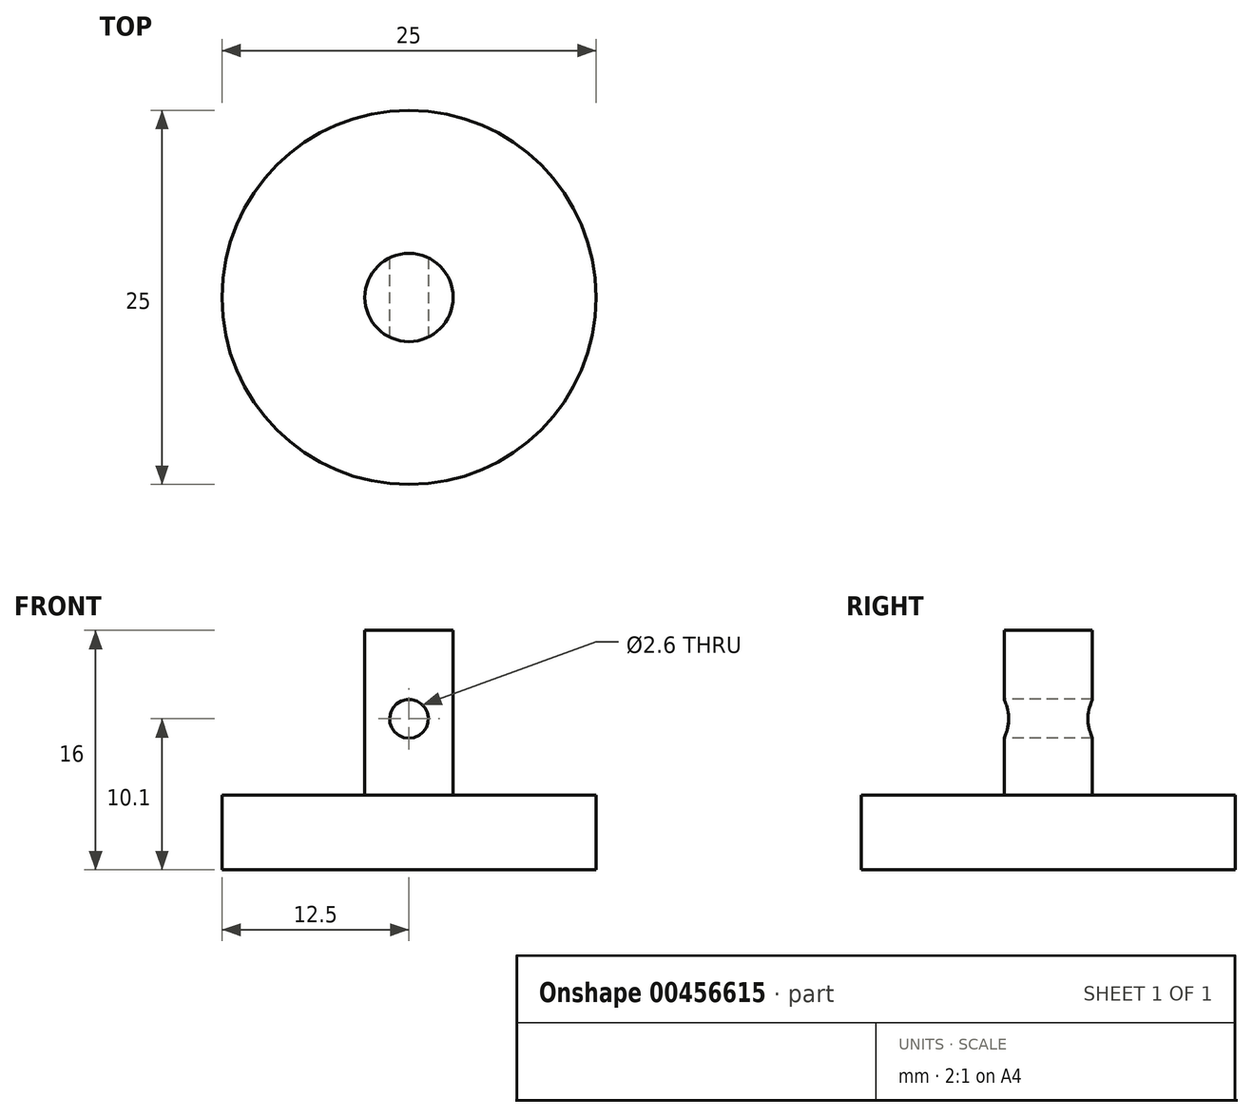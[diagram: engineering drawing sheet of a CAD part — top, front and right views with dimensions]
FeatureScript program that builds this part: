
annotation { "Feature Type Name" : "Feature", "Feature Type Description" : "" }
export const myFeature = defineFeature(function(context is Context, id is Id, definition is map)
    precondition{}
    {
        {
            assignVariable(context, id + "F0", {"name" : "L", "anyValue" : 5 * mm});
        }
        {
            var Q0;
            Q0=qCreatedBy(makeId("Top.planeOp"),FACE);
            var sketch = newSketch(context, id + "F1", { "sketchPlane" : qUnion([Q0])});
            skCircle(sketch, "E0", {"center": v(0, 0) * mm, "radius": 12.5 * mm});
            skSolve(sketch);
        }
        {
            var Q0;
            Q0=makeQuery(id+"F1.imprint","IMPRINT",FACE,{"disambiguationData":[TD([[makeQuery(id+"F1.imprint","IMPRINT",EDGE,{"derivedFrom":sQuery(id+"F1.wireOp",EDGE,"E0")}),1.0]])]});
            var Q1;
            Q1=sQuery(id+"F1.wireOp",EDGE,"E0");
            extrude(context, id + "F2", {"entities" : qUnion([Q0]), "surfaceEntities" : qUnion([Q1]), "offsetDistance" : 25 * mm, "depth" : getVariable(context, 'L')});
        }
        {
            assignVariable(context, id + "F3", {"name" : "d", "anyValue" : 5.9 * mm});
        }
        {
            assignVariable(context, id + "F4", {"name" : "l", "anyValue" : 11 * mm});
        }
        {
            var Q0;
            Q0=makeQuery(id+"F2.opExtrude","CAP_FACE",FACE,{"disambiguationData":[OSD([sQuery(id+"F1.wireOp",EDGE,"E0")])],"isStart":false});
            var sketch = newSketch(context, id + "F5", { "sketchPlane" : qUnion([Q0])});
            skCircle(sketch, "E1", {"center": v(0, 0) * mm, "radius": 2.95 * mm});
            skLineSegment(sketch, "E2", {"start": v(0, 0) * mm, "end": v(0, -2.95) * mm});
            skLineSegment(sketch, "E3", {"start": v(0, 0) * mm, "end": v(-2.95, 0) * mm});
            skSolve(sketch);
        }
        {
            var Q0;
            Q0=makeQuery(id+"F5.imprint","IMPRINT",FACE,{"disambiguationData":[TD([[makeQuery(id+"F5.imprint","IMPRINT",EDGE,{"derivedFrom":sQuery(id+"F5.wireOp",EDGE,"E1")}),1.0]])]});
            var Q1;
            Q1=sQuery(id+"F5.wireOp",EDGE,"E1");
            extrude(context, id + "F6", {"entities" : qUnion([Q0]), "surfaceEntities" : qUnion([Q1]), "depth" : getVariable(context, 'l')});
        }
        {
            var Q0;
            Q0=qCreatedBy(makeId("Front.planeOp"),FACE);
            cPlane(context, id + "F7", {"entities" : qUnion([Q0]), "cplaneType" : CPlaneType.OFFSET, "offset" : getVariable(context, 'd') / 2, "width" : 150 * mm, "height" : 150 * mm});
        }
        {
            var Q0;
            Q0=qCreatedBy(id+"F7.planeOp",FACE);
            var sketch = newSketch(context, id + "F8", { "sketchPlane" : qUnion([Q0])});
            skLineSegment(sketch, "E4", {"start": v(0, 10.1) * mm, "end": v(0, 5) * mm});
            skCircle(sketch, "E5", {"center": v(0, 10.1) * mm, "radius": 1.3 * mm});
            skSolve(sketch);
        }
        {
            var Q0;
            Q0=makeQuery(id+"F8.imprint","IMPRINT",FACE,{"disambiguationData":[TD([[makeQuery(id+"F8.imprint","IMPRINT",EDGE,{"derivedFrom":sQuery(id+"F8.wireOp",EDGE,"E5")}),1.0]])]});
            var Q1;
            Q1=sQuery(id+"F8.wireOp",EDGE,"E5");
            extrude(context, id + "F9", {"entities" : qUnion([Q0]), "operationType" : NewBodyOperationType.REMOVE, "surfaceEntities" : qUnion([Q1]), "endBound" : BoundingType.THROUGH_ALL, "oppositeDirection" : true, "depth" : 25 * mm});
        }
    });
